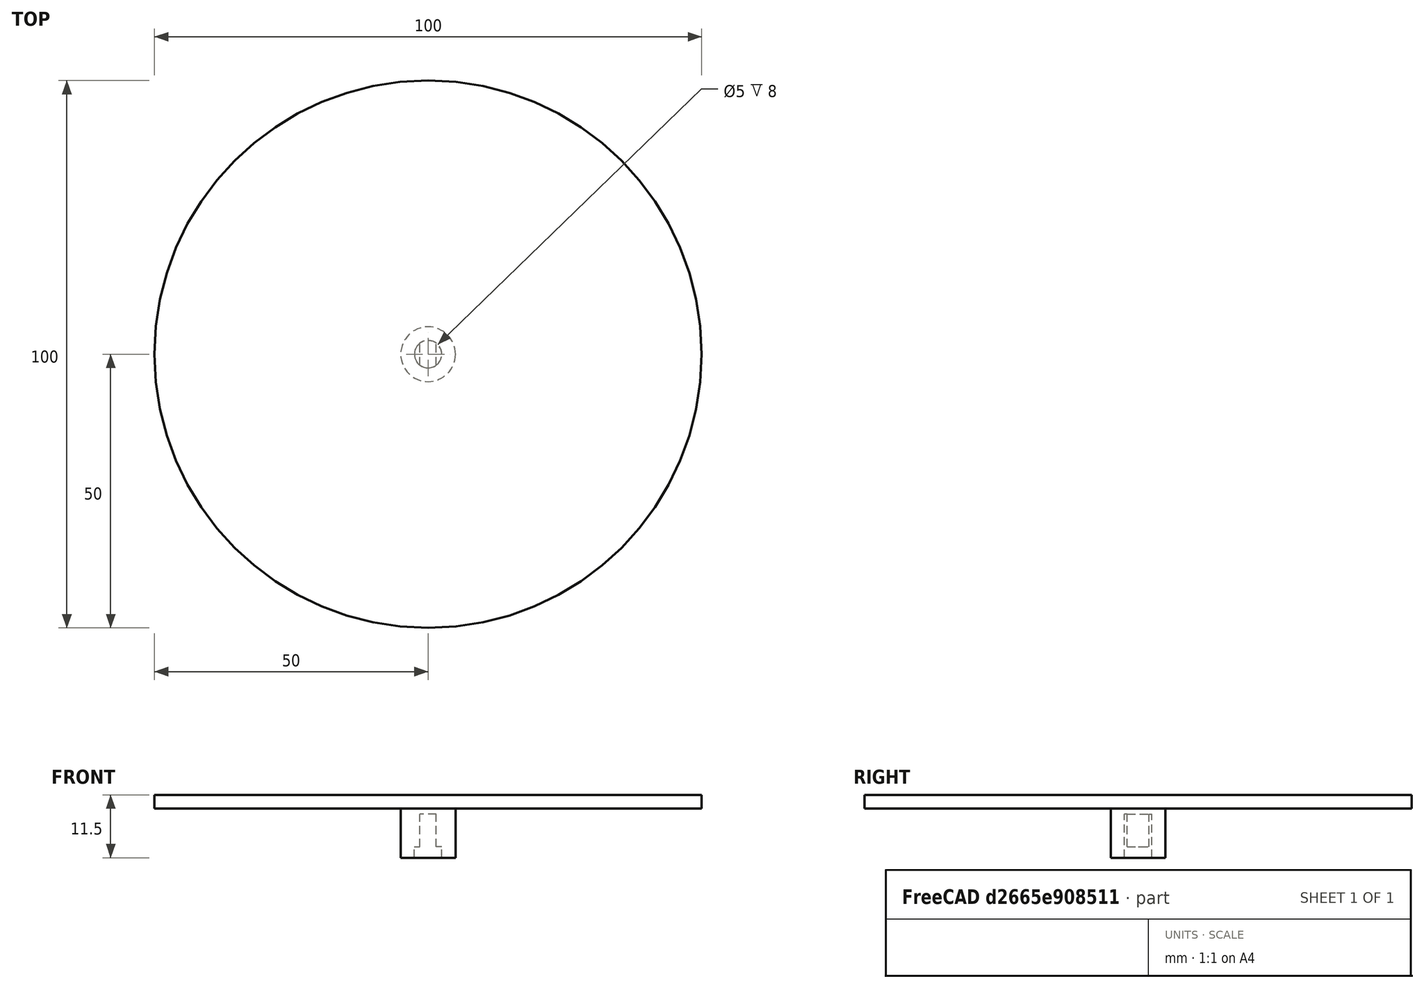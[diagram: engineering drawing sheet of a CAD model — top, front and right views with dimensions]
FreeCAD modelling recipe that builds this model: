
FCSTD DOCUMENT  (FreeCAD 0.16R6706 (Git))
Label: S2H-bottom-motor-plate
License: All rights reserved
LicenseURL: http://en.wikipedia.org/wiki/All_rights_reserved
objects: Part::Cylinder×9, Part::Cut×5, Part::Box×4, Part::MultiFuse×3
note: 21 computed .brp shape members not serialized (recipe doc carries the construction recipe); baked Part::Feature solids carry a one-line shape summary decoded from their .brp

FEATURE [Part::Cylinder] Cylinder019
  Angle = 360
  Height = 2.5
  Placement = pos=(0,0,20) rot=(0,0,1;0rad)
  Radius = 50
FEATURE [Part::Cylinder] Cylinder020
  Angle = 360
  Height = 9
  Placement = pos=(0,0,11) rot=(0,0,1;0rad)
  Radius = 5
FEATURE [Part::Cylinder] Cylinder021
  Angle = 360
  Height = 19
  Radius = 14
FEATURE [Part::Cylinder] Cylinder022
  Angle = 360
  Height = 1.5
  Placement = pos=(-8,0,19) rot=(0,0,1;0rad)
  Radius = 4.5
FEATURE [Part::Cylinder] Cylinder023
  Angle = 360
  Height = 8.5
  Placement = pos=(-8,0,20.5) rot=(0,0,1;0rad)
  Radius = 2.5
FEATURE [Part::Cylinder] Cylinder024
  Angle = 360
  Height = 2
  Placement = pos=(0,-17.5,18) rot=(0,0,1;0rad)
  Radius = 2.1
FEATURE [Part::Cylinder] Cylinder025
  Angle = 360
  Height = 2
  Placement = pos=(0,17.5,18) rot=(0,0,1;0rad)
  Radius = 2.1
FEATURE [Part::Cylinder] Cylinder026
  Angle = 360
  Height = 0.75
  Placement = pos=(0,-17.5,18) rot=(0,0,1;0rad)
  Radius = 3.5
FEATURE [Part::Cylinder] Cylinder027
  Angle = 360
  Height = 0.75
  Placement = pos=(0,17.5,18) rot=(0,0,1;0rad)
  Radius = 3.5
FEATURE [Part::Box] Box011  label="Cube011"
  Height = 0.75
  Length = 7
  Placement = pos=(-3.5,-17.5,18) rot=(0,0,1;0rad)
  Width = 35
FEATURE [Part::MultiFuse] Fusion005
  Placement = pos=(0,0,0.25) rot=(0,0,1;0rad)
  Shapes = -> [Cylinder026,Cylinder027,Box011]
FEATURE [Part::Cut] Cut009
  Base = -> Fusion005
  Tool = -> Cylinder024
FEATURE [Part::Cut] Cut010
  Base = -> Cut009
  Tool = -> Cylinder025
FEATURE [Part::Box] Box012  label="Cube012"
  Height = 16.5
  Length = 17
  Placement = pos=(0,-7.3,2.5) rot=(0,0,1;0rad)
  Width = 14.6
FEATURE [Part::Box] Box013  label="Cube013"
  Height = 6
  Length = 1
  Placement = pos=(-6.5,-2.5,23) rot=(0,0,1;0rad)
  Width = 5
FEATURE [Part::Box] Box014  label="Cube014"
  Height = 6
  Length = 1
  Placement = pos=(-10.5,-2.5,23) rot=(0,0,1;0rad)
  Width = 5
FEATURE [Part::Cut] Cut011
  Base = -> Cylinder023
  Tool = -> Box013
FEATURE [Part::Cut] Cut012
  Base = -> Cut011
  Tool = -> Box014
FEATURE [Part::MultiFuse] Fusion006
  Placement = pos=(8,0,-10) rot=(0,0,1;0rad)
  Shapes = -> [Cut012,Box012,Cut010,Cylinder022,Cylinder021]
FEATURE [Part::Cut] Cut013
  Base = -> Cylinder020
  Tool = -> Fusion006
FEATURE [Part::MultiFuse] Fusion007  label="bottom plate"
  Shapes = -> [Cylinder019,Cut013]
